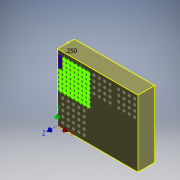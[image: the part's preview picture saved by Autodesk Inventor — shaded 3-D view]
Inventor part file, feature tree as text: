
AUTODESK INVENTOR PART (.ipt)
format: ipt  version: 2018 (Build 220112000, 112)  size: 3,514,880 bytes
history: native  units: mm (DEFAULTED — no unit token found)
features: other x427, loft x121, extrude x18, fillet x5, sketch x4
ambient origin geometry x8: Origin, YZ Plane, XZ Plane, XY Plane, X Axis, Y Axis, Z Axis, Center Point
bodies: Solid1 (feature_tree)
feature tree (575):
  extrude  "Extrusion1"  Depth=127.254mm
  sketch  "Sketch2"  dims[d2=32.004mm d3=0.0mm d4=5.2578mm]
  extrude  "Extrusion2"  Depth=5.2578mm
  extrude  "Extrusion3"  Depth=7.5692mm
  sketch  "Sketch3"  dims[d5=11.6713mm d6=7.5692mm]
  extrude  "Extrusion4"  Depth=7.5692mm
  extrude  "Extrusion5"  Depth=5.2578mm
  extrude  "Extrusion6"  Depth=7.5692mm
  fillet  "Fillet1"  Radius=7.5692mm
  loft  "Loft1"
  loft  "Loft2"
  loft  "Loft3"
  loft  "Loft4"
  loft  "Loft5"
  loft  "Loft6"
  loft  "Loft7"
  loft  "Loft8"
  loft  "Loft9"
  loft  "Loft10"
  loft  "Loft11"
  loft  "Loft12"
  loft  "Loft13"
  loft  "Loft14"
  loft  "Loft15"
  loft  "Loft16"
  loft  "Loft17"
  loft  "Loft18"
  loft  "Loft19"
  loft  "Loft20"
  loft  "Loft21"
  loft  "Loft22"
  loft  "Loft23"
  loft  "Loft24"
  loft  "Loft25"
  loft  "Loft26"
  loft  "Loft27"
  loft  "Loft28"
  loft  "Loft29"
  loft  "Loft30"
  loft  "Loft31"
  loft  "Loft32"
  loft  "Loft33"
  loft  "Loft34"
  loft  "Loft35"
  loft  "Loft36"
  loft  "Loft37"
  loft  "Loft38"
  loft  "Loft39"
  loft  "Loft40"
  loft  "Loft41"
  loft  "Loft42"
  loft  "Loft43"
  loft  "Loft44"
  loft  "Loft45"
  loft  "Loft46"
  loft  "Loft47"
  loft  "Loft48"
  loft  "Loft49"
  loft  "Loft50"
  loft  "Loft51"
  loft  "Loft52"
  loft  "Loft53"
  loft  "Loft54"
  loft  "Loft55"
  loft  "Loft56"
  loft  "Loft57"
  loft  "Loft58"
  loft  "Loft59"
  loft  "Loft60"
  loft  "Loft61"
  loft  "Loft62"
  loft  "Loft63"
  loft  "Loft64"
  sketch  "Sketch4"  dims[d7=5.26mm d8=7.5692mm d9=5.2578mm d10=7.5692mm d11=7.5692mm d12=5.2578mm d13=7.5692mm d14=7.5692mm d15=7.5692mm d16=7.5692mm d17=7.5692mm d18=7.5692mm d19=7.5692mm d20=7.5692mm d21=7.5692mm d22=7.5692mm d23=3.6576mm d24=14.6558mm d25=0.0mm d26=3.6576mm d27=3.6576mm d28=3.6576mm d29=3.6576mm d30=3.6576mm d31=3.6576mm d32=3.6576mm d33=3.6576mm d34=3.6576mm d35=3.6576mm d36=3.6576mm d37=3.6576mm d38=3.6576mm d39=3.6576mm d40=3.6576mm d41=3.6576mm d42=3.6576mm d43=3.6576mm d44=3.6576mm d45=3.6576mm d46=3.6576mm d47=3.6576mm d48=3.6576mm d49=3.6576mm d50=3.6576mm d51=3.6576mm d52=3.6576mm d53=3.6576mm d54=3.6576mm d55=3.6576mm d56=3.6576mm d57=3.6576mm d58=3.6576mm d59=3.6576mm d60=3.6576mm d61=3.6576mm d62=3.6576mm d63=3.6576mm d64=3.6576mm d65=3.6576mm d66=3.6576mm d67=3.6576mm d68=3.6576mm d69=3.6576mm d70=3.6576mm d71=3.6576mm d72=3.6576mm d73=3.6576mm d74=3.6576mm d75=3.6576mm d76=3.6576mm d77=3.6576mm d78=3.6576mm d79=5.8166mm d80=3.6576mm d81=3.6576mm d82=3.6576mm d83=3.6576mm d84=3.6576mm d85=3.6576mm d86=3.6576mm d87=3.6576mm d88=3.6576mm d89=3.6576mm d90=19.812mm d91=0.0mm d92=6.35mm d93=5.8166mm d94=5.8166mm d95=5.8166mm d96=5.8166mm d97=5.8166mm d98=5.8166mm d99=5.8166mm d100=5.8166mm d101=5.8166mm d102=5.8166mm d103=5.8166mm d104=5.8166mm d105=5.8166mm d106=5.8166mm d107=5.8166mm d108=5.8166mm d109=5.8166mm d110=5.8166mm d111=5.8166mm d112=5.8166mm d113=5.8166mm d114=5.8166mm d115=5.8166mm d116=5.8166mm d117=5.8166mm d118=5.8166mm d119=5.8166mm d120=5.8166mm d121=5.8166mm d122=5.8166mm d123=5.8166mm d124=5.8166mm d125=5.8166mm d126=5.8166mm d127=5.8166mm d128=5.8166mm d129=5.8166mm d130=5.8166mm d131=5.8166mm d132=5.8166mm d133=5.8166mm d134=5.8166mm d135=5.8166mm d136=5.8166mm d137=5.8166mm d138=3.6576mm d139=5.8166mm d140=5.8166mm d141=5.8166mm d142=5.8166mm d143=5.8166mm d144=5.8166mm d145=5.8166mm d146=5.8166mm d147=5.8166mm d148=5.8166mm d149=5.8166mm d150=5.8166mm d151=5.8166mm d152=5.8166mm d153=5.8166mm d154=5.8166mm d155=5.8166mm d156=5.8166mm d159=9.398mm d160=0.0mm d161=6.2738mm d162=6.2738mm d163=6.2738mm d164=6.2738mm d165=6.2738mm d166=6.2738mm d167=6.2738mm d168=6.2738mm d169=6.2738mm d170=6.2738mm d171=6.2738mm d172=6.2738mm d173=6.2738mm d174=6.2738mm d175=6.2738mm d176=6.2738mm d177=6.2738mm d178=6.2738mm d179=6.2738mm d180=6.2738mm d181=6.2738mm d182=6.2738mm d183=6.2738mm d184=6.2738mm d185=6.2738mm d186=6.2738mm d187=6.2738mm d188=6.2738mm d189=6.2738mm d190=6.2738mm d191=6.2738mm d192=6.2738mm d193=6.2738mm d194=6.2738mm d195=6.2738mm d196=6.2738mm d197=6.2738mm d198=6.2738mm d199=6.2738mm d200=6.2738mm d201=6.2738mm d202=6.2738mm d203=6.2738mm d204=6.2738mm d205=6.2738mm d206=6.2738mm d207=6.2738mm d208=6.2738mm d209=6.2738mm d210=6.2738mm d211=6.2738mm d212=6.2738mm d213=6.2738mm d214=6.2738mm d215=6.2738mm d216=6.2738mm d217=6.2738mm d218=6.2738mm d219=6.2738mm d220=6.2738mm d221=6.2738mm d222=6.2738mm d223=6.2738mm d224=6.2738mm d225=9.398mm d226=0.0mm d227=6.9596mm d228=6.9596mm d229=6.9596mm d230=6.9596mm d231=6.9596mm d232=6.9596mm d233=6.9596mm d234=6.9596mm d235=6.9596mm d236=6.9596mm d237=6.9596mm d238=6.9596mm d239=6.9596mm d240=6.9596mm d241=6.9596mm d242=6.9596mm d243=6.9596mm d244=6.9596mm d245=6.9596mm d246=6.9596mm d247=6.9596mm d248=6.9596mm d249=6.9596mm d250=6.9596mm d251=6.9596mm d252=6.9596mm d253=6.9596mm d254=6.9596mm d255=6.9596mm d256=6.9596mm d257=6.9596mm d258=6.9596mm d259=6.9596mm d260=6.9596mm d261=6.9596mm d262=6.9596mm d263=6.9596mm d264=6.9596mm d265=6.9596mm d266=6.9596mm d267=6.9596mm d268=6.9596mm d269=6.9596mm d270=6.9596mm d271=6.9596mm d272=6.9596mm d273=6.9596mm d274=6.9596mm d275=6.9596mm d276=6.9596mm d277=6.9596mm d278=6.9596mm d279=6.9596mm d280=6.9596mm d281=6.9596mm d282=6.9596mm d283=6.9596mm d284=6.9596mm d285=6.9596mm d286=6.9596mm d287=6.9596mm d288=6.9596mm d289=6.9596mm d290=6.9596mm d291=4.1148mm d292=0.0mm d293=1.8288mm d294=0.0mm d295=90.0deg d296=0.0mm d297=90.0deg d298=0.0mm d299=90.0deg d300=0.0mm d301=90.0deg d302=0.0mm d303=90.0deg d304=0.0mm d305=90.0deg d306=0.0mm d307=90.0deg d308=0.0mm d309=90.0deg d310=0.0mm d311=90.0deg d312=0.0mm d313=90.0deg d314=0.0mm d315=90.0deg d316=0.0mm d317=90.0deg d318=0.0mm d319=90.0deg d320=0.0mm d321=90.0deg d322=0.0mm d323=90.0deg d324=0.0mm d325=90.0deg d326=0.0mm d327=90.0deg d328=0.0mm d329=90.0deg d330=0.0mm d331=90.0deg d332=0.0mm d333=90.0deg d334=0.0mm d335=90.0deg d336=0.0mm d337=90.0deg d338=0.0mm d339=90.0deg d340=0.0mm d341=90.0deg d342=0.0mm d343=90.0deg d344=0.0mm d345=90.0deg d346=0.0mm d347=90.0deg d348=0.0mm d349=90.0deg d350=0.0mm d351=90.0deg d352=0.0mm d353=90.0deg d354=0.0mm d355=90.0deg d356=0.0mm d357=90.0deg d358=0.0mm d359=90.0deg d360=0.0mm d361=90.0deg d362=0.0mm d363=90.0deg d364=0.0mm d365=90.0deg d366=0.0mm d367=90.0deg d368=0.0mm d369=90.0deg d370=0.0mm d371=90.0deg d372=0.0mm d373=90.0deg d374=0.0mm d375=90.0deg d376=0.0mm d377=90.0deg d378=0.0mm d379=90.0deg d380=0.0mm d381=90.0deg d382=0.0mm d383=90.0deg d384=0.0mm d385=90.0deg d386=0.0mm d387=90.0deg d388=0.0mm d389=90.0deg d390=0.0mm d391=90.0deg d392=0.0mm d393=90.0deg d394=0.0mm d395=90.0deg d396=0.0mm d397=90.0deg d398=0.0mm d399=90.0deg d400=0.0mm d401=90.0deg d402=0.0mm d403=90.0deg d404=0.0mm d405=90.0deg d406=0.0mm d407=90.0deg d408=0.0mm d409=90.0deg d410=0.0mm d411=90.0deg d412=0.0mm d413=90.0deg d414=0.0mm d415=90.0deg d416=0.0mm d417=90.0deg d418=0.0mm d419=90.0deg d420=0.0mm d421=90.0deg d422=0.0mm d423=90.0deg d424=0.0mm d425=90.0deg d426=0.0mm d427=90.0deg d428=0.0mm d429=90.0deg d430=0.0mm d431=90.0deg d432=0.0mm d433=90.0deg d434=0.0mm d435=90.0deg d436=0.0mm d437=90.0deg d438=0.0mm d439=90.0deg d440=0.0mm d441=90.0deg d442=0.0mm d443=90.0deg d444=0.0mm d445=90.0deg d446=0.0mm d447=90.0deg d448=0.0mm d449=90.0deg d450=0.0mm d451=90.0deg d452=0.0mm d453=90.0deg d454=0.0mm d455=90.0deg d456=0.0mm d457=90.0deg d458=0.0mm d459=90.0deg d460=0.0mm d461=90.0deg d462=0.0mm d463=90.0deg d464=0.0mm d465=90.0deg d466=0.0mm d467=90.0deg d468=0.0mm d469=90.0deg d470=0.0mm d471=90.0deg d472=0.0mm d473=90.0deg d474=0.0mm d475=90.0deg d476=0.0mm d477=90.0deg d478=0.0mm d479=90.0deg d480=0.0mm d481=90.0deg d482=0.0mm d483=90.0deg d484=0.0mm d485=90.0deg d486=0.0mm d487=90.0deg d488=0.0mm d489=90.0deg d490=0.0mm d491=90.0deg d492=0.0mm d493=90.0deg d494=0.0mm d495=90.0deg d496=0.0mm d497=90.0deg d498=0.0mm d499=90.0deg d500=0.0mm d501=90.0deg d502=0.0mm d503=90.0deg d504=0.0mm d505=90.0deg d506=0.0mm d507=90.0deg d508=0.0mm d509=90.0deg d510=0.0mm d511=90.0deg d512=0.0mm d513=90.0deg d514=0.0mm d515=90.0deg d516=0.0mm d517=90.0deg d518=0.0mm d519=90.0deg d520=0.0mm d521=90.0deg d522=0.0mm d523=90.0deg d524=0.0mm d525=90.0deg d526=0.0mm d527=90.0deg d528=0.0mm d529=90.0deg d530=0.0mm d531=90.0deg d532=0.0mm d533=90.0deg d534=0.0mm d535=90.0deg d536=0.0mm d537=90.0deg d538=0.0mm d539=90.0deg d540=0.0mm d541=90.0deg d542=0.0mm d543=90.0deg d544=0.0mm d545=90.0deg d546=0.0mm d547=90.0deg d548=0.0mm d549=90.0deg d550=0.0mm d551=90.0deg d552=0.0mm d553=90.0deg d554=0.0mm d555=90.0deg d556=0.0mm d557=90.0deg d558=0.0mm d559=90.0deg d560=0.0mm d561=90.0deg d562=0.0mm d563=90.0deg d564=0.0mm d565=90.0deg d566=0.0mm d567=90.0deg d568=0.0mm d569=90.0deg d570=0.0mm d571=90.0deg d572=0.0mm d573=90.0deg d574=0.0mm d575=90.0deg d576=0.0mm d577=90.0deg d578=0.0mm d579=90.0deg d580=0.0mm d581=90.0deg d582=0.0mm d583=90.0deg d584=0.0mm d585=90.0deg d586=0.0mm d587=90.0deg d588=0.0mm d589=90.0deg d590=0.0mm d591=90.0deg d592=0.0mm d593=90.0deg d594=0.0mm d595=90.0deg d596=0.0mm d597=90.0deg d598=0.0mm d599=90.0deg d600=0.0mm d601=90.0deg d602=0.0mm d603=90.0deg d604=0.0mm d605=90.0deg d606=0.0mm d607=90.0deg d608=0.0mm d609=90.0deg d610=0.0mm d611=90.0deg d612=0.0mm d613=90.0deg d614=0.0mm d615=90.0deg d616=0.0mm d617=90.0deg d618=0.0mm d619=90.0deg d620=0.0mm d621=90.0deg d622=0.0mm d623=90.0deg d624=0.0mm d625=90.0deg d626=0.0mm d627=90.0deg d628=0.0mm d629=90.0deg d630=0.0mm d631=90.0deg d632=0.0mm d633=90.0deg d634=0.0mm d635=90.0deg d636=0.0mm d637=90.0deg d638=0.0mm d639=90.0deg d640=0.0mm d641=90.0deg d642=0.0mm d643=90.0deg d644=0.0mm d645=90.0deg d646=0.0mm d647=90.0deg d648=0.0mm d649=90.0deg d650=0.0mm d651=90.0deg d652=0.0mm d653=90.0deg d654=0.0mm d655=90.0deg d656=0.0mm d657=90.0deg d658=0.0mm d659=90.0deg d660=0.0mm d661=90.0deg d662=0.0mm d663=90.0deg d664=0.0mm d665=90.0deg d666=0.0mm d667=90.0deg d668=0.0mm d669=90.0deg d670=0.0mm d671=90.0deg d672=0.0mm d673=90.0deg d674=0.0mm d675=90.0deg d676=0.0mm d677=90.0deg d678=0.0mm d679=90.0deg d680=0.0mm d681=90.0deg d682=0.0mm d683=90.0deg d684=0.0mm d685=90.0deg d686=0.0mm d687=90.0deg d688=0.0mm d689=90.0deg d690=0.0mm d691=90.0deg d692=0.0mm d693=90.0deg d694=0.0mm d695=90.0deg d696=0.0mm d697=90.0deg d698=0.0mm d699=90.0deg d700=0.0mm d701=90.0deg d702=0.0mm d703=90.0deg d704=0.0mm d705=90.0deg d706=0.0mm d707=90.0deg d708=0.0mm d709=90.0deg d710=0.0mm d711=90.0deg d712=0.0mm d713=90.0deg d714=0.0mm d715=90.0deg d716=0.0mm d717=90.0deg d718=0.0mm d719=90.0deg d720=0.0mm d721=90.0deg d722=0.0mm d723=90.0deg d724=0.0mm d725=90.0deg d726=0.0mm d727=90.0deg d728=0.0mm d729=90.0deg d730=0.0mm d731=90.0deg d732=0.0mm d733=90.0deg d734=0.0mm d735=90.0deg d736=0.0mm d737=90.0deg d738=0.0mm d739=90.0deg d740=0.0mm d741=90.0deg d742=0.0mm d743=90.0deg d744=0.0mm d745=90.0deg d746=0.0mm d747=90.0deg d748=0.0mm d749=90.0deg d750=0.0mm d751=90.0deg d752=0.0mm d753=90.0deg d754=0.0mm d755=90.0deg d756=0.0mm d757=90.0deg d758=0.0mm d759=90.0deg d760=0.0mm d761=90.0deg d762=0.0mm d763=90.0deg d764=0.0mm d765=90.0deg d766=0.0mm d767=90.0deg d768=0.0mm d769=90.0deg d770=0.0mm d771=90.0deg d772=0.0mm d773=90.0deg d774=0.0mm d775=90.0deg d776=0.0mm d777=90.0deg d778=0.0mm d779=90.0deg d780=0.0mm d781=90.0deg d782=0.0mm d783=90.0deg d784=0.0mm d785=90.0deg d786=0.0mm d787=90.0deg d788=0.0mm d789=90.0deg d790=0.0mm d791=90.0deg d792=0.0mm d793=90.0deg d794=0.0mm d795=90.0deg d796=0.0mm d797=90.0deg d798=0.0mm d799=90.0deg d800=0.0mm d801=90.0deg d802=0.0mm d803=90.0deg d804=0.0mm d805=90.0deg d806=10.16mm d807=10.16mm d808=10.16mm d809=10.16mm d810=10.16mm d811=10.16mm d812=10.16mm d813=3.3147mm d814=3.3147mm d815=3.3147mm d816=3.3147mm d817=3.3147mm d818=3.3147mm d819=3.3147mm d820=3.3147mm d821=3.3147mm d822=3.3147mm d823=3.3147mm d824=3.3147mm d825=3.3147mm d826=3.3147mm d827=3.3147mm d828=3.3147mm d829=5.6642mm d830=5.6642mm d831=5.6642mm d832=5.6642mm d833=5.6642mm d834=5.6642mm d835=5.6642mm d836=5.6642mm d837=5.6642mm d838=5.6642mm d839=5.6642mm d840=5.6642mm d841=5.6642mm d842=5.6642mm d843=5.6642mm d844=5.6642mm d845=6.2865mm d846=19.6215mm d847=0.0mm d848=9.2837mm d849=0.0mm d850=0.8128mm d851=0.00254mm d852=0.0mm d853=0.0mm d854=90.0deg d855=0.0mm d856=90.0deg d857=0.0mm d858=90.0deg d859=6.2865mm d860=6.2865mm d861=6.2865mm d862=6.2865mm d863=6.2865mm d864=6.2865mm d865=6.2865mm d866=6.2865mm d867=6.2865mm d868=6.2865mm d869=6.2865mm d870=6.2865mm d871=6.2865mm d872=6.2865mm d873=6.2865mm d874=19.6215mm d875=0.0mm d876=9.2837mm d877=0.0mm d878=0.00254mm d879=0.0mm d880=0.8128mm d881=0.0mm d882=90.0deg d883=0.0mm d884=90.0deg d885=0.0mm d886=90.0deg d887=0.0mm d888=90.0deg d889=0.0mm d890=90.0deg d891=0.0mm d892=90.0deg d893=0.0mm d894=90.0deg d895=0.0mm d896=90.0deg d897=0.0mm d898=90.0deg d899=0.0mm d900=90.0deg d901=0.0mm d902=90.0deg d903=0.0mm d904=90.0deg d905=0.0mm d906=90.0deg d907=0.0mm d908=90.0deg d909=0.0mm d910=90.0deg d911=0.0mm d912=90.0deg d913=0.0mm d914=90.0deg d915=0.0mm d916=90.0deg d917=0.0mm d918=90.0deg d919=0.0mm d920=90.0deg d921=0.0mm d922=90.0deg d923=0.0mm d924=90.0deg d925=0.0mm d926=90.0deg d927=0.0mm d928=90.0deg d929=0.0mm d930=90.0deg d931=0.0mm d932=90.0deg d933=0.0mm d934=90.0deg d935=0.0mm d936=90.0deg d937=0.0mm d938=90.0deg d939=0.0mm d940=90.0deg d941=0.0mm d942=90.0deg d943=0.0mm d944=90.0deg d945=0.0mm d946=90.0deg d947=0.0mm d948=90.0deg d949=0.0mm d950=90.0deg d951=0.0mm d952=90.0deg d953=0.0mm d954=90.0deg d955=0.0mm d956=90.0deg d957=0.0mm d958=90.0deg d959=0.0mm d960=90.0deg d961=0.0mm d962=90.0deg d963=0.0mm d964=90.0deg d965=0.0mm d966=90.0deg d967=0.0mm d968=90.0deg d969=0.0mm d970=90.0deg d971=16.51mm d972=10.16mm d973=10.16mm d974=10.16mm d975=6.2865mm d976=6.2865mm d977=6.2865mm d978=6.2865mm d979=6.2865mm d980=6.2865mm d981=6.2865mm d982=6.2865mm d983=6.2865mm d984=6.2865mm d985=6.2865mm d986=6.2865mm d987=6.2865mm d988=6.2865mm d989=6.2865mm d990=6.2865mm d991=5.6642mm d992=5.6642mm d993=5.6642mm d994=5.6642mm d995=5.6642mm d996=5.6642mm d997=5.6642mm d998=5.6642mm d999=5.6642mm d1000=5.6642mm d1001=5.6642mm d1002=5.6642mm d1003=5.6642mm d1004=5.6642mm d1005=5.6642mm d1006=5.6642mm d1007=3.3147mm d1008=3.3147mm d1009=3.3147mm d1010=3.3147mm d1011=3.3147mm d1012=3.3147mm d1013=3.3147mm d1014=3.3147mm d1015=3.3147mm d1016=3.3147mm d1017=3.3147mm d1018=3.3147mm d1019=3.3147mm d1020=3.3147mm d1021=3.3147mm d1022=3.3147mm d1023=20.1803mm d1024=0.0mm d1025=9.2837mm d1026=0.0mm d1027=0.00254mm d1028=0.0mm d1029=0.8128mm d1030=0.0mm d1031=90.0deg d1032=0.0mm d1033=90.0deg d1034=0.0mm d1035=90.0deg d1036=0.0mm d1037=90.0deg d1038=0.0mm d1039=90.0deg d1040=0.0mm d1041=90.0deg d1042=0.0mm d1043=90.0deg d1044=0.0mm d1045=90.0deg d1046=0.0mm d1047=90.0deg d1048=0.0mm d1049=90.0deg d1050=0.0mm d1051=90.0deg d1052=0.0mm d1053=90.0deg d1054=0.0mm d1055=90.0deg d1056=0.0mm d1057=90.0deg d1058=0.0mm d1059=90.0deg d1060=0.0mm d1061=90.0deg d1062=0.0mm d1063=90.0deg d1064=0.0mm d1065=90.0deg d1066=0.0mm d1067=90.0deg d1068=0.0mm d1069=90.0deg d1070=0.0mm d1071=90.0deg d1072=0.0mm d1073=90.0deg d1074=0.0mm d1075=90.0deg d1076=0.0mm d1077=90.0deg d1078=0.0mm d1079=90.0deg d1080=0.0mm d1081=90.0deg d1082=0.0mm d1083=90.0deg d1084=0.0mm d1085=90.0deg d1086=0.0mm d1087=90.0deg d1088=0.0mm d1089=90.0deg d1090=0.0mm d1091=90.0deg d1092=0.0mm d1093=90.0deg d1094=0.0mm d1095=90.0deg d1096=0.0mm d1097=90.0deg d1098=0.0mm d1099=90.0deg d1100=0.0mm d1101=90.0deg d1102=0.0mm d1103=90.0deg d1104=0.0mm d1105=90.0deg d1106=0.0mm d1107=90.0deg d1108=0.0mm d1109=90.0deg d1110=0.0mm d1111=90.0deg d1112=0.0mm d1113=90.0deg d1114=0.0mm d1115=90.0deg d1116=0.0mm d1117=90.0deg d1118=0.0mm d1119=90.0deg d1120=0.0mm d1121=90.0deg d1122=0.0mm d1123=90.0deg d1124=0.0mm d1125=90.0deg d1126=10.16mm d1127=10.16mm d1128=10.16mm d1129=10.16mm d1130=10.16mm d1131=10.16mm d1132=10.16mm d1133=10.16mm d1134=10.16mm d1135=10.16mm d1136=10.16mm d1137=10.16mm d1138=6.2865mm d1139=6.2865mm d1140=6.2865mm d1141=6.2865mm d1142=6.2865mm d1143=6.2865mm d1144=6.2865mm d1145=6.2865mm d1146=6.2865mm d1147=6.2865mm d1148=6.2865mm d1149=6.2865mm d1150=6.2865mm d1151=6.2865mm d1152=6.2865mm d1153=6.2865mm d1154=10.16mm d1155=10.16mm d1156=6.2865mm d1157=6.2865mm d1158=6.2865mm d1159=6.2865mm d1160=6.2865mm d1161=6.2865mm d1162=6.2865mm d1163=6.2865mm d1164=6.2865mm d1165=5.6642mm d1166=5.6642mm d1167=5.6642mm d1168=5.6642mm d1169=5.6642mm d1170=5.6642mm d1171=5.6642mm d1172=5.6642mm d1173=5.6642mm d1174=5.6642mm d1175=5.6642mm d1176=5.6642mm d1177=5.6642mm d1178=5.6642mm d1179=5.6642mm d1180=5.6642mm d1181=5.6642mm d1182=5.6642mm d1183=5.6642mm d1184=5.6642mm d1185=5.6642mm d1186=5.6642mm d1187=5.6642mm d1188=5.6642mm d1189=5.6642mm d1190=3.3147mm d1191=3.3147mm d1192=3.3147mm d1193=3.3147mm d1194=3.3147mm d1195=3.3147mm d1196=3.3147mm d1197=3.3147mm d1198=3.3147mm d1199=3.3147mm d1200=3.3147mm d1201=3.3147mm d1202=3.3147mm d1203=3.3147mm d1204=3.3147mm d1205=3.3147mm d1206=3.3147mm d1207=3.3147mm d1208=3.3147mm d1209=3.3147mm d1210=3.3147mm d1211=3.3147mm d1212=3.3147mm d1213=3.3147mm d1214=3.3147mm d1215=20.1803mm d1216=0.0mm d1217=9.2837mm d1218=0.0mm d1219=0.00254mm d1220=0.0mm d1221=0.8128mm d1222=0.0mm d1223=90.0deg d1224=0.0mm d1225=90.0deg d1226=0.0mm d1227=90.0deg d1228=0.0mm d1229=90.0deg d1230=0.0mm d1231=90.0deg d1232=0.0mm d1233=90.0deg d1234=0.0mm d1235=90.0deg d1236=0.0mm d1237=90.0deg d1238=0.0mm d1239=90.0deg d1240=0.0mm d1241=90.0deg d1242=0.0mm d1243=90.0deg d1244=0.0mm d1245=90.0deg d1246=0.0mm d1247=90.0deg d1248=0.0mm d1249=90.0deg d1250=0.0mm d1251=90.0deg d1252=0.0mm d1253=90.0deg d1254=0.0mm d1255=90.0deg d1256=0.0mm d1257=90.0deg d1258=0.0mm d1259=90.0deg d1260=0.0mm d1261=90.0deg d1262=0.0mm d1263=90.0deg d1264=0.0mm d1265=90.0deg d1266=0.0mm d1267=90.0deg d1268=0.0mm d1269=90.0deg d1270=0.0mm d1271=90.0deg d1272=0.0mm d1273=90.0deg d1274=0.0mm d1275=90.0deg d1276=0.0mm d1277=90.0deg d1278=0.0mm d1279=90.0deg d1280=0.0mm d1281=90.0deg d1282=0.0mm d1283=90.0deg d1284=0.0mm d1285=90.0deg d1286=0.0mm d1287=90.0deg d1288=0.0mm d1289=90.0deg d1290=0.0mm d1291=90.0deg d1292=0.0mm d1293=90.0deg d1294=0.0mm d1295=90.0deg d1296=0.0mm d1297=90.0deg d1298=0.0mm d1299=90.0deg d1300=0.0mm d1301=90.0deg d1302=0.0mm d1303=90.0deg d1304=0.0mm d1305=90.0deg d1306=0.0mm d1307=90.0deg d1308=0.0mm d1309=90.0deg d1310=0.0mm d1311=90.0deg d1312=0.0mm d1313=90.0deg d1314=0.0mm d1315=90.0deg d1316=0.0mm d1317=90.0deg d1318=0.0mm d1319=90.0deg d1320=0.0mm d1321=90.0deg d1322=0.0mm d1323=90.0deg d1324=0.0mm d1325=90.0deg d1326=0.0mm d1327=90.0deg d1328=0.0mm d1329=90.0deg d1330=0.0mm d1331=90.0deg d1332=0.0mm d1333=90.0deg d1334=0.0mm d1335=90.0deg d1336=0.0mm d1337=90.0deg d1338=0.0mm d1339=90.0deg d1340=0.0mm d1341=90.0deg d1342=0.0mm d1343=90.0deg d1344=0.0mm d1345=90.0deg d1346=0.0mm d1347=90.0deg d1348=0.0mm d1349=90.0deg d1350=0.0mm d1351=90.0deg d1352=0.0mm d1353=90.0deg d1354=0.0mm d1355=90.0deg d1356=0.0mm d1357=90.0deg d1358=0.0mm d1359=90.0deg d1360=0.0mm d1361=90.0deg d1362=0.0mm d1363=90.0deg d1364=0.0mm d1365=90.0deg d1366=0.0mm d1367=90.0deg d1368=0.0mm d1369=90.0deg d1370=0.0mm d1371=90.0deg]
  extrude  "Extrusion7"  Depth=3.6576mm
  extrude  "Extrusion8"  Depth=3.6576mm
  fillet  "Fillet2"  Radius=5.8166mm
  extrude  "Extrusion9"  Depth=3.6576mm
  loft  "Loft65"
  extrude  "Extrusion10"  Depth=3.6576mm
  extrude  "Extrusion11"  Depth=3.6576mm
  extrude  "Extrusion12"  Depth=3.6576mm
  fillet  "Fillet3"  Radius=3.6576mm
  loft  "Loft66"
  loft  "Loft67"
  loft  "Loft68"
  loft  "Loft69"
  loft  "Loft70"
  loft  "Loft71"
  loft  "Loft72"
  loft  "Loft73"
  loft  "Loft74"
  loft  "Loft75"
  loft  "Loft76"
  loft  "Loft77"
  loft  "Loft78"
  loft  "Loft79"
  loft  "Loft80"
  extrude  "Extrusion13"  Depth=5.8166mm
  extrude  "Extrusion14"  Depth=5.8166mm
  extrude  "Extrusion15"  Depth=5.8166mm
  fillet  "Fillet4"  Radius=5.8166mm
  loft  "Loft81"
  loft  "Loft82"
  loft  "Loft83"
  loft  "Loft84"
  loft  "Loft85"
  loft  "Loft86"
  loft  "Loft87"
  loft  "Loft88"
  loft  "Loft89"
  loft  "Loft90"
  loft  "Loft91"
  loft  "Loft92"
  loft  "Loft93"
  loft  "Loft94"
  loft  "Loft95"
  loft  "Loft96"
  extrude  "Extrusion16"  Depth=5.8166mm
  extrude  "Extrusion17"  Depth=5.8166mm
  extrude  "Extrusion18"  Depth=5.8166mm
  fillet  "Fillet5"  Radius=5.8166mm
  loft  "Loft97"
  loft  "Loft98"
  loft  "Loft99"
  loft  "Loft100"
  loft  "Loft101"
  loft  "Loft102"
  loft  "Loft103"
  loft  "Loft104"
  loft  "Loft105"
  loft  "Loft106"
  loft  "Loft107"
  loft  "Loft108"
  loft  "Loft109"
  loft  "Loft110"
  loft  "Loft111"
  loft  "Loft112"
  loft  "Loft113"
  loft  "Loft114"
  loft  "Loft115"
  loft  "Loft116"
  loft  "Loft117"
  loft  "Loft118"
  loft  "Loft119"
  loft  "Loft120"
  loft  "Loft121"
  sketch  "Sketch1"  dims[d0=153.162mm d1=127.254mm]
  other  "Edges1"
  other  "Edges2"
  other  "Edges3"
  other  "Edges4"
  other  "Edges5"
  other  "Edges6"
  other  "Edges7"
  other  "Edges8"
  other  "Edges9"
  other  "Edges10"
  other  "Edges11"
  other  "Edges12"
  other  "Edges13"
  other  "Edges14"
  other  "Edges15"
  other  "Edges16"
  other  "Edges17"
  other  "Edges18"
  other  "Edges19"
  other  "Edges20"
  other  "Edges21"
  other  "Edges22"
  other  "Edges23"
  other  "Edges24"
  other  "Edges25"
  other  "Edges26"
  other  "Edges27"
  other  "Edges28"
  other  "Edges29"
  other  "Edges30"
  other  "Edges31"
  other  "Edges32"
  other  "Edges33"
  other  "Edges34"
  other  "Edges35"
  other  "Edges36"
  other  "Edges37"
  other  "Edges38"
  other  "Edges39"
  other  "Edges40"
  other  "Edges41"
  other  "Edges42"
  other  "Edges43"
  other  "Edges44"
  other  "Edges45"
  other  "Edges46"
  other  "Edges47"
  other  "Edges48"
  other  "Edges49"
  other  "Edges50"
  other  "Edges51"
  other  "Edges52"
  other  "Edges53"
  other  "Edges54"
  other  "Edges55"
  other  "Edges56"
  other  "Edges57"
  other  "Edges58"
  other  "Edges59"
  other  "Edges60"
  other  "Edges61"
  other  "Edges62"
  other  "Edges63"
  other  "Edges64"
  other  "Edges65"
  other  "Edges66"
  other  "Edges67"
  other  "Edges68"
  other  "Edges69"
  other  "Edges70"
  other  "Edges71"
  other  "Edges72"
  other  "Edges73"
  other  "Edges74"
  other  "Edges75"
  other  "Edges76"
  other  "Edges77"
  other  "Edges78"
  other  "Edges79"
  other  "Edges80"
  other  "Edges81"
  other  "Edges82"
  other  "Edges83"
  other  "Edges84"
  other  "Edges85"
  other  "Edges86"
  other  "Edges87"
  other  "Edges88"
  other  "Edges89"
  other  "Edges90"
  other  "Edges91"
  other  "Edges92"
  other  "Edges93"
  other  "Edges94"
  other  "Edges95"
  other  "Edges96"
  other  "Edges97"
  other  "Edges98"
  other  "Edges99"
  other  "Edges100"
  other  "Edges101"
  other  "Edges102"
  other  "Edges103"
  other  "Edges104"
  other  "Edges105"
  other  "Edges106"
  other  "Edges107"
  other  "Edges108"
  other  "Edges109"
  other  "Edges110"
  other  "Edges111"
  other  "Edges112"
  other  "Edges113"
  other  "Edges114"
  other  "Edges115"
  other  "Edges116"
  other  "Edges117"
  other  "Edges118"
  other  "Edges119"
  other  "Edges120"
  other  "Edges121"
  other  "Edges122"
  other  "Edges123"
  other  "Edges124"
  other  "Edges125"
  other  "Edges126"
  other  "Edges127"
  other  "Edges128"
  other  "Edges129"
  other  "Edges130"
  other  "Edges131"
  other  "Edges132"
  other  "Edges133"
  other  "Edges134"
  other  "Edges135"
  other  "Edges136"
  other  "Edges137"
  other  "Edges138"
  other  "Edges139"
  other  "Edges140"
  other  "Edges141"
  other  "Edges142"
  other  "Edges143"
  other  "Edges144"
  other  "Edges145"
  other  "Edges146"
  other  "Edges147"
  other  "Edges148"
  other  "Edges149"
  other  "Edges150"
  other  "Edges151"
  other  "Edges152"
  other  "Edges153"
  other  "Edges154"
  other  "Edges155"
  other  "Edges156"
  other  "Edges157"
  other  "Edges158"
  other  "Edges159"
  other  "Edges160"
  other  "Edges161"
  other  "Edges162"
  other  "Edges163"
  other  "Edges164"
  other  "Edges165"
  other  "Edges166"
  other  "Edges167"
  other  "Edges168"
  other  "Edges169"
  other  "Edges170"
  other  "Edges171"
  other  "Edges172"
  other  "Edges173"
  other  "Edges174"
  other  "Edges175"
  other  "Edges176"
  other  "Edges177"
  other  "Edges178"
  other  "Edges179"
  other  "Edges180"
  other  "Edges181"
  other  "Edges182"
  other  "Edges183"
  other  "Edges184"
  other  "Edges185"
  other  "Edges186"
  other  "Edges187"
  other  "Edges188"
  other  "Edges189"
  other  "Edges190"
  other  "Edges191"
  other  "Edges192"
  other  "Edges193"
  other  "Edges194"
  other  "Edges195"
  other  "Edges196"
  other  "Edges197"
  other  "Edges198"
  other  "Edges199"
  other  "Edges200"
  other  "Edges201"
  other  "Edges202"
  other  "Edges203"
  other  "Edges204"
  other  "Edges205"
  other  "Edges206"
  other  "Edges207"
  other  "Edges208"
  other  "Edges209"
  other  "Edges210"
  other  "Edges211"
  other  "Edges212"
  other  "Edges213"
  other  "Edges214"
  other  "Edges215"
  other  "Edges216"
  other  "Edges217"
  other  "Edges218"
  other  "Edges219"
  other  "Edges220"
  other  "Edges221"
  other  "Edges222"
  other  "Edges223"
  other  "Edges224"
  other  "Edges225"
  other  "Edges226"
  other  "Edges227"
  other  "Edges228"
  other  "Edges229"
  other  "Edges230"
  other  "Edges231"
  other  "Edges232"
  other  "Edges233"
  other  "Edges234"
  other  "Edges235"
  other  "Edges236"
  other  "Edges237"
  other  "Edges238"
  other  "Edges239"
  other  "Edges240"
  other  "Edges241"
  other  "Edges242"
  other  "Edges243"
  other  "Edges244"
  other  "Edges245"
  other  "Edges246"
  other  "Edges247"
  other  "Edges248"
  other  "Edges249"
  other  "Edges250"
  other  "Edges251"
  other  "Edges252"
  other  "Edges253"
  other  "Edges254"
  other  "Edges255"
  other  "Edges256"
  other  "Edges257"
  other  "Edges258"
  other  "Edges259"
  other  "Edges260"
  other  "Edges261"
  other  "Edges262"
  other  "Edges263"
  other  "Edges264"
  other  "Edges265"
  other  "Edges266"
  other  "Edges267"
  other  "Edges268"
  other  "Edges269"
  other  "Edges270"
  other  "Edges271"
  other  "Edges272"
  other  "Edges273"
  other  "Edges274"
  other  "Edges275"
  other  "Edges276"
  other  "Edges277"
  other  "Edges278"
  other  "Edges279"
  other  "Edges280"
  other  "Edges281"
  other  "Edges282"
  other  "Edges283"
  other  "Edges284"
  other  "Edges285"
  other  "Edges286"
  other  "Edges287"
  other  "Edges288"
  other  "Edges289"
  other  "Edges290"
  other  "Edges291"
  other  "Edges292"
  other  "Edges293"
  other  "Edges294"
  other  "Edges295"
  other  "Edges296"
  other  "Edges297"
  other  "Edges298"
  other  "Edges299"
  other  "Edges300"
  other  "Edges301"
  other  "Edges302"
  other  "Edges303"
  other  "Edges304"
  other  "Edges305"
  other  "Edges306"
  other  "Edges307"
  other  "Edges308"
  other  "Edges309"
  other  "Edges310"
  other  "Edges311"
  other  "Edges312"
  other  "Edges313"
  other  "Edges314"
  other  "Edges315"
  other  "Edges316"
  other  "Edges317"
  other  "Edges318"
  other  "Edges319"
  other  "Edges320"
  other  "Edges321"
  other  "Edges322"
  other  "Edges323"
  other  "Edges324"
  other  "Edges325"
  other  "Edges326"
  other  "Edges327"
  other  "Edges328"
  other  "Edges329"
  other  "Edges330"
  other  "Edges331"
  other  "Edges332"
  other  "Edges333"
  other  "Edges334"
  other  "Edges335"
  other  "Edges336"
  other  "Edges337"
  other  "Edges338"
  other  "Edges339"
  other  "Edges340"
  other  "Edges341"
  other  "Edges342"
  other  "Edges343"
  other  "Edges344"
  other  "Edges345"
  other  "Edges346"
  other  "Edges347"
  other  "Edges348"
  other  "Edges349"
  other  "Edges350"
  other  "Edges351"
  other  "Edges352"
  other  "Edges353"
  other  "Edges354"
  other  "Edges355"
  other  "Edges356"
  other  "Edges357"
  other  "Edges358"
  other  "Edges359"
  other  "Edges360"
  other  "Edges361"
  other  "Edges362"
  other  "Edges363"
  other  "Edges364"
  other  "Edges365"
  other  "Edges366"
  other  "Edges367"
  other  "Edges368"
  other  "Edges369"
  other  "Edges370"
  other  "Edges371"
  other  "Edges372"
  other  "Edges373"
  other  "Edges374"
  other  "Edges375"
  other  "Edges376"
  other  "Edges377"
  other  "Edges378"
  other  "Edges379"
  other  "Edges380"
  other  "Edges381"
  other  "Edges382"
  other  "Edges383"
  other  "Edges384"
  other  "Edges385"
  other  "Edges386"
  other  "Edges387"
  other  "Edges388"
  other  "Edges389"
  other  "Edges390"
  other  "Edges391"
  other  "Edges392"
  other  "Edges393"
  other  "Edges394"
  other  "Edges395"
  other  "Edges396"
  other  "Edges397"
  other  "Edges398"
  other  "Edges399"
  other  "Edges400"
  other  "Edges401"
  other  "Edges402"
  other  "Edges403"
  other  "Edges404"
  other  "Edges405"
  other  "Edges406"
  other  "Edges407"
  other  "Edges408"
  other  "Edges409"
  other  "Edges410"
  other  "Edges411"
  other  "Edges412"
  other  "Edges413"
  other  "Edges414"
  other  "Edges415"
  other  "Edges416"
  other  "Edges417"
  other  "Edges418"
  other  "Edges419"
  other  "Edges420"
  other  "Edges421"
  other  "Edges422"
  other  "Edges423"
  other  "Edges424"
  other  "Edges425"
  other  "Edges426"
  other  "Edges427"
